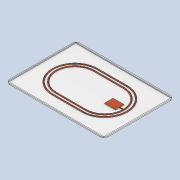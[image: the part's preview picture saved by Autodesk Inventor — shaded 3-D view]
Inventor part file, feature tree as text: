
AUTODESK INVENTOR PART (.ipt)
format: ipt  version: 2021 (Build 250183000, 183)  size: 431,616 bytes
history: native  units: mm
features: fillet x5, extrude x3, sketch x3, plane x1
ambient origin geometry x8: Origin, YZ Plane, XZ Plane, XY Plane, X Axis, Y Axis, Z Axis, Center Point
bodies: Solid1 (feature_tree)
feature tree (12):
  extrude  "Extrusion1"  Depth=88.9mm
  extrude  "Extrusion2"  Depth=0.8mm TaperAngle=0.0deg
  extrude  "Extrusion3"  Depth=10.0mm
  fillet  "Fillet3"  Radius=30.0mm
  fillet  "Fillet4"  Radius=30.0mm
  fillet  "Fillet5"  Radius=10.0mm
  fillet  "Fillet6"  Radius=0.6mm
  fillet  "Fillet7"  Radius=0.5mm
  plane  "Work Plane2"
  sketch  "Sketch1"  dims[d0=63.5mm d1=88.9mm]
  sketch  "Sketch2"  dims[d2=1.0mm d3=0.0mm d6=0.8mm d7=0.0mm]
  sketch  "Sketch3"  dims[d8=10.0mm d9=10.0mm d10=30.0mm d11=30.0mm d12=10.0mm d13=0.6mm d14=0.0mm d15=0.5mm d16=0.5mm d17=0.3mm d32=3.0mm d33=3.0mm d35=5.0mm]
